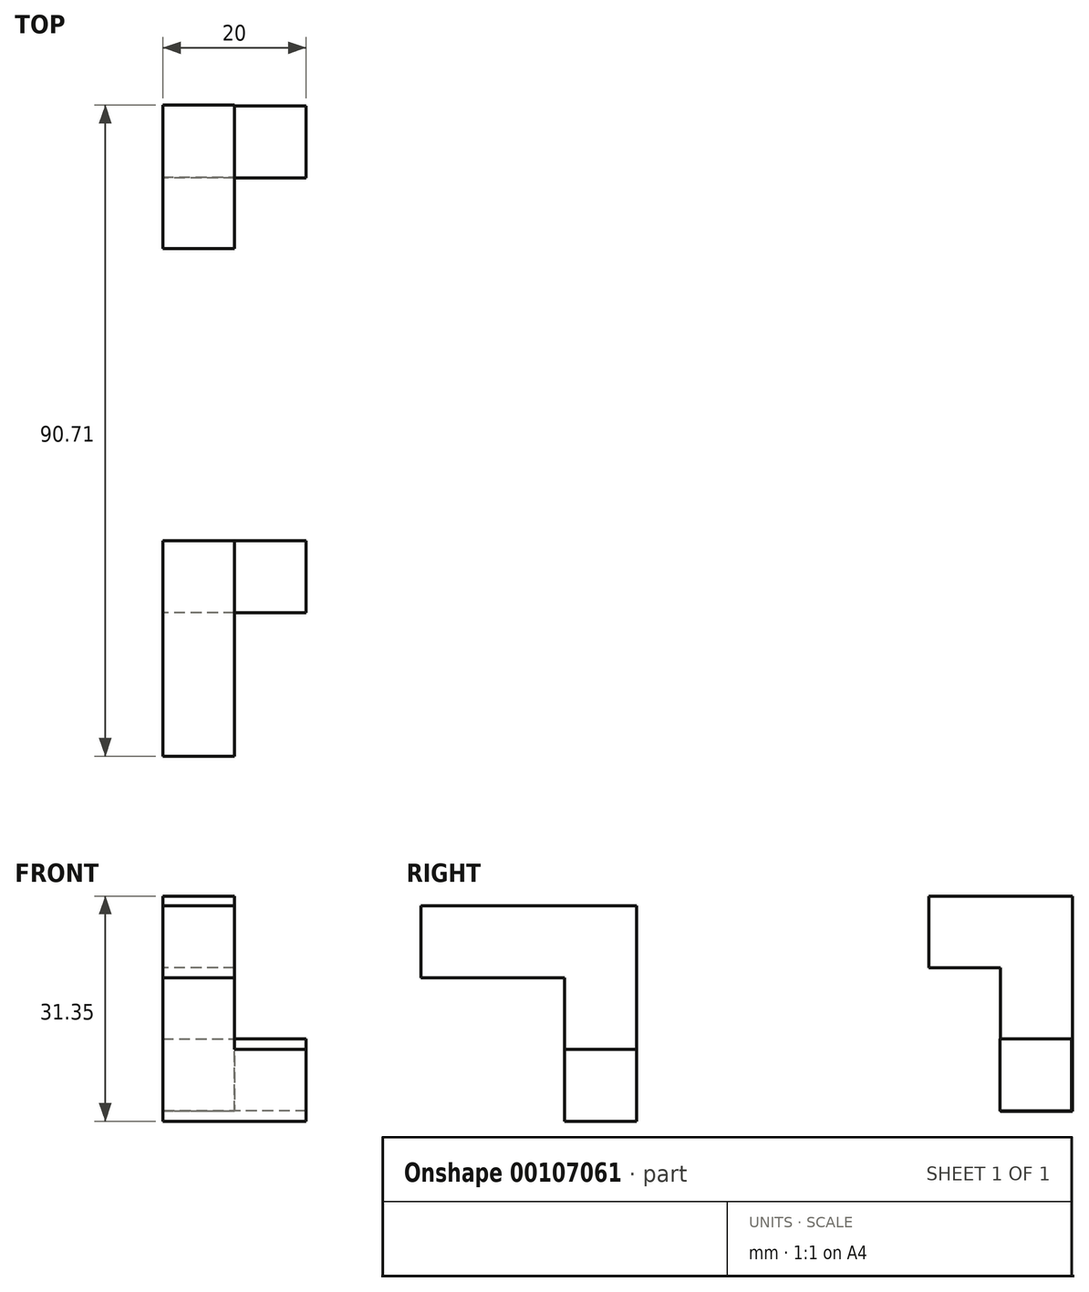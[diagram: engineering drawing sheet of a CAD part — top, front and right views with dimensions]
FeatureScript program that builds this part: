
annotation { "Feature Type Name" : "Feature", "Feature Type Description" : "" }
export const myFeature = defineFeature(function(context is Context, id is Id, definition is map)
    precondition{}
    {
        {
            var Q0;
            Q0=qCreatedBy(makeId("Right.planeOp"),FACE);
            var sketch = newSketch(context, id + "F0", { "sketchPlane" : qUnion([Q0])});
            skLineSegment(sketch, "E0", {"start": v(-56.96, 48.53) * mm, "end": v(-26.96, 48.53) * mm});
            skLineSegment(sketch, "E1", {"start": v(-26.96, 48.53) * mm, "end": v(-26.96, 18.53) * mm});
            skLineSegment(sketch, "E2", {"start": v(-26.96, 18.53) * mm, "end": v(-36.96, 18.53) * mm});
            skLineSegment(sketch, "E3", {"start": v(-36.96, 18.53) * mm, "end": v(-36.96, 38.53) * mm});
            skLineSegment(sketch, "E4", {"start": v(-36.96, 38.53) * mm, "end": v(-56.96, 38.53) * mm});
            skLineSegment(sketch, "E5", {"start": v(-56.96, 38.53) * mm, "end": v(-56.96, 48.53) * mm});
            skSolve(sketch);
        }
        {
            var Q0;
            Q0=makeQuery(id+"F0.imprint","IMPRINT",FACE,{"disambiguationData":[TD([[makeQuery(id+"F0.imprint","IMPRINT",EDGE,{"derivedFrom":sQuery(id+"F0.wireOp",EDGE,"E0")}),-1.0]])]});
            extrude(context, id + "F1", {"entities" : qUnion([Q0]), "depth" : 10 * mm});
        }
        {
            var Q0;
            Q0=makeQuery(id+"F1.opExtrude","CAP_FACE",FACE,{"disambiguationData":[OSD([sQuery(id+"F0.wireOp",EDGE,"E0"),sQuery(id+"F0.wireOp",EDGE,"E1"),sQuery(id+"F0.wireOp",EDGE,"E2"),sQuery(id+"F0.wireOp",EDGE,"E3"),sQuery(id+"F0.wireOp",EDGE,"E4"),sQuery(id+"F0.wireOp",EDGE,"E5")])],"isStart":false});
            var sketch = newSketch(context, id + "F2", { "sketchPlane" : qUnion([Q0])});
            skLineSegment(sketch, "E6.bottom", {"start": v(-36.96, 18.53) * mm, "end": v(-26.96, 18.53) * mm});
            skLineSegment(sketch, "E6.top", {"start": v(-36.96, 28.53) * mm, "end": v(-26.96, 28.53) * mm});
            skLineSegment(sketch, "E6.left", {"start": v(-36.96, 18.53) * mm, "end": v(-36.96, 28.53) * mm});
            skLineSegment(sketch, "E6.right", {"start": v(-26.96, 18.53) * mm, "end": v(-26.96, 28.53) * mm});
            skSolve(sketch);
        }
        {
            var Q0;
            Q0=makeQuery(id+"F2.imprint","IMPRINT",FACE,{"disambiguationData":[TD([[makeQuery(id+"F2.imprint","IMPRINT",EDGE,{"derivedFrom":sQuery(id+"F2.wireOp",EDGE,"E6.bottom")}),-1.0]])]});
            extrude(context, id + "F3", {"entities" : qUnion([Q0]), "operationType" : NewBodyOperationType.ADD, "depth" : 10 * mm});
        }
        {
            var Q0;
            Q0=qCreatedBy(makeId("Right.planeOp"),FACE);
            var sketch = newSketch(context, id + "F4", { "sketchPlane" : qUnion([Q0])});
            skLineSegment(sketch, "E7", {"start": v(13.75, 49.88) * mm, "end": v(13.75, 39.88) * mm});
            skLineSegment(sketch, "E8", {"start": v(13.75, 39.88) * mm, "end": v(23.75, 39.88) * mm});
            skLineSegment(sketch, "E9", {"start": v(23.75, 39.88) * mm, "end": v(23.75, 19.88) * mm});
            skLineSegment(sketch, "E10", {"start": v(23.75, 19.88) * mm, "end": v(33.75, 19.88) * mm});
            skLineSegment(sketch, "E11", {"start": v(33.75, 19.88) * mm, "end": v(33.75, 49.88) * mm});
            skLineSegment(sketch, "E12", {"start": v(33.75, 49.88) * mm, "end": v(13.75, 49.88) * mm});
            skSolve(sketch);
        }
        {
            var Q0;
            Q0 = qSketchRegion(id + "F4", true);
            extrude(context, id + "F5", {"entities" : qUnion([Q0]), "depth" : 10 * mm});
        }
        {
            var Q0;
            Q0=qCreatedBy(makeId("Right.planeOp"),FACE);
            var sketch = newSketch(context, id + "F6", { "sketchPlane" : qUnion([Q0])});
            skLineSegment(sketch, "E13.bottom", {"start": v(23.63, 19.97) * mm, "end": v(33.63, 19.97) * mm});
            skLineSegment(sketch, "E13.top", {"start": v(23.63, 29.97) * mm, "end": v(33.63, 29.97) * mm});
            skLineSegment(sketch, "E13.left", {"start": v(23.63, 19.97) * mm, "end": v(23.63, 29.97) * mm});
            skLineSegment(sketch, "E13.right", {"start": v(33.63, 19.97) * mm, "end": v(33.63, 29.97) * mm});
            skSolve(sketch);
        }
        {
            var Q0;
            Q0 = qSketchRegion(id + "F6", true);
            extrude(context, id + "F7", {"entities" : qUnion([Q0]), "operationType" : NewBodyOperationType.ADD, "depth" : 20 * mm});
        }
    });
